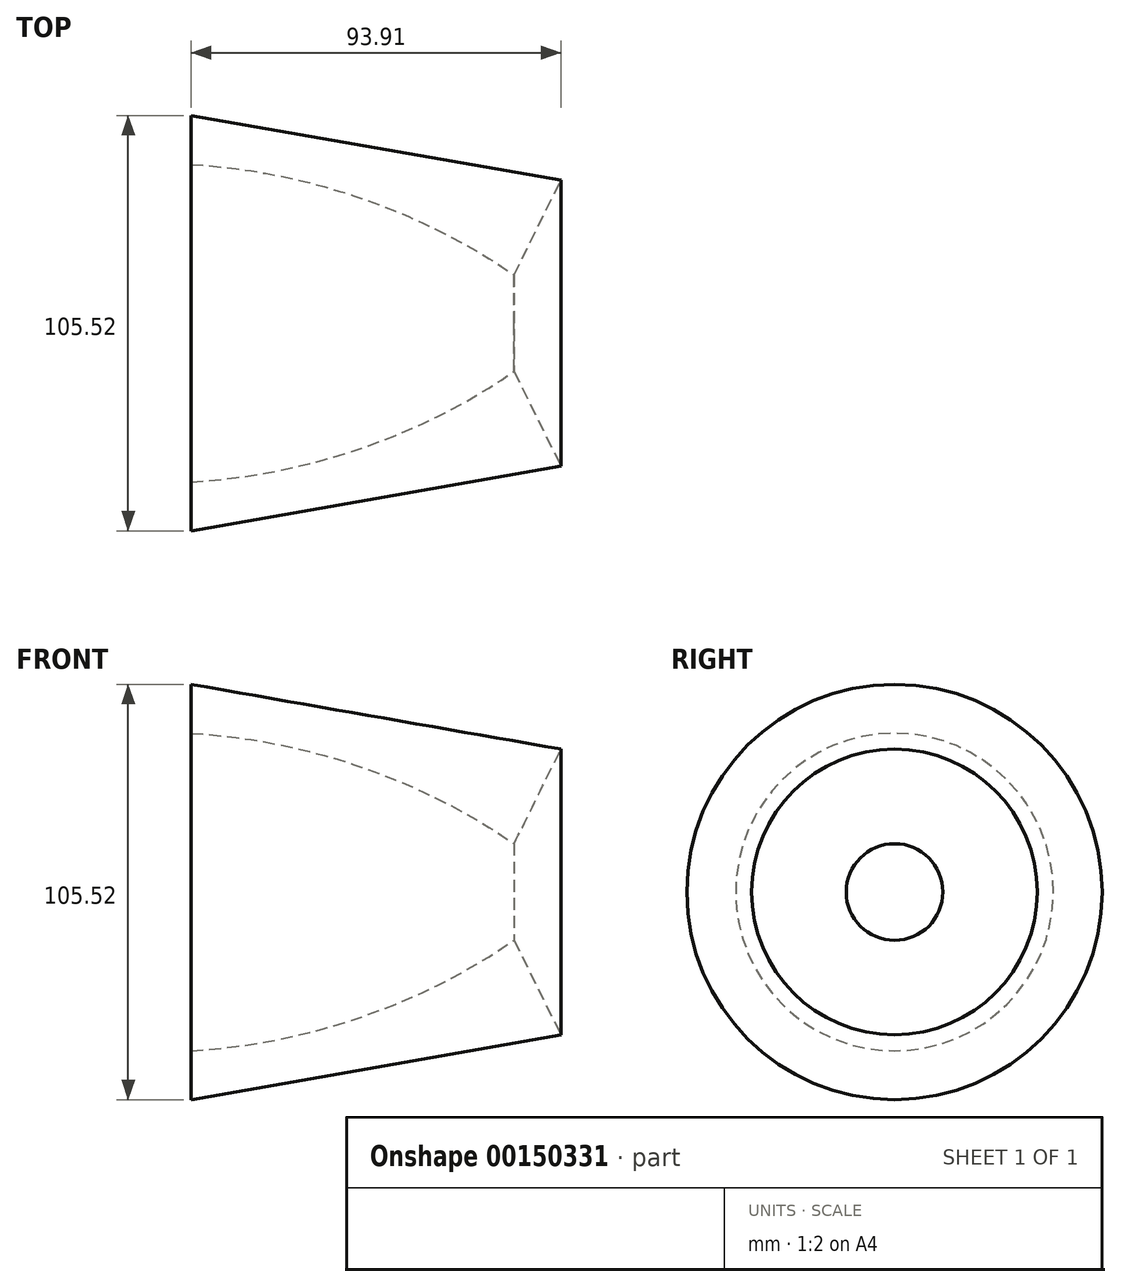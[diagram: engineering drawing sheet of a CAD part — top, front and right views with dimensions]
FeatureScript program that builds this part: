
annotation { "Feature Type Name" : "Feature", "Feature Type Description" : "" }
export const myFeature = defineFeature(function(context is Context, id is Id, definition is map)
    precondition{}
    {
        {
            var Q0;
            Q0=qCreatedBy(makeId("Front.planeOp"),FACE);
            var sketch = newSketch(context, id + "F0", { "sketchPlane" : qUnion([Q0])});
            skArc(sketch, "E0", {"start": v(82.03, 12.28) * mm, "mid": v(42.92, 31.86) * mm, "end": v(0, 40.34) * mm});
            skLineSegment(sketch, "E1", {"start": v(0, 40.34) * mm, "end": v(0, 52.76) * mm});
            skLineSegment(sketch, "E2", {"start": v(0, 52.76) * mm, "end": v(93.9, 36.3) * mm});
            skLineSegment(sketch, "E3", {"start": v(93.9, 36.3) * mm, "end": v(82.03, 12.28) * mm});
            skLineSegment(sketch, "E4", {"start": v(0, 0) * mm, "end": v(45.87, 0) * mm});
            skSolve(sketch);
        }
        {
            var Q0;
            Q0 = qSketchRegion(id + "F0", true);
            var Q1;
            Q1=sQuery(id+"F0.wireOp",EDGE,"E4");
            revolve(context, id + "F1", {"entities" : qUnion([Q0]), "axis" : qUnion([Q1]), "revolveType" : RevolveType.FULL});
        }
    });
